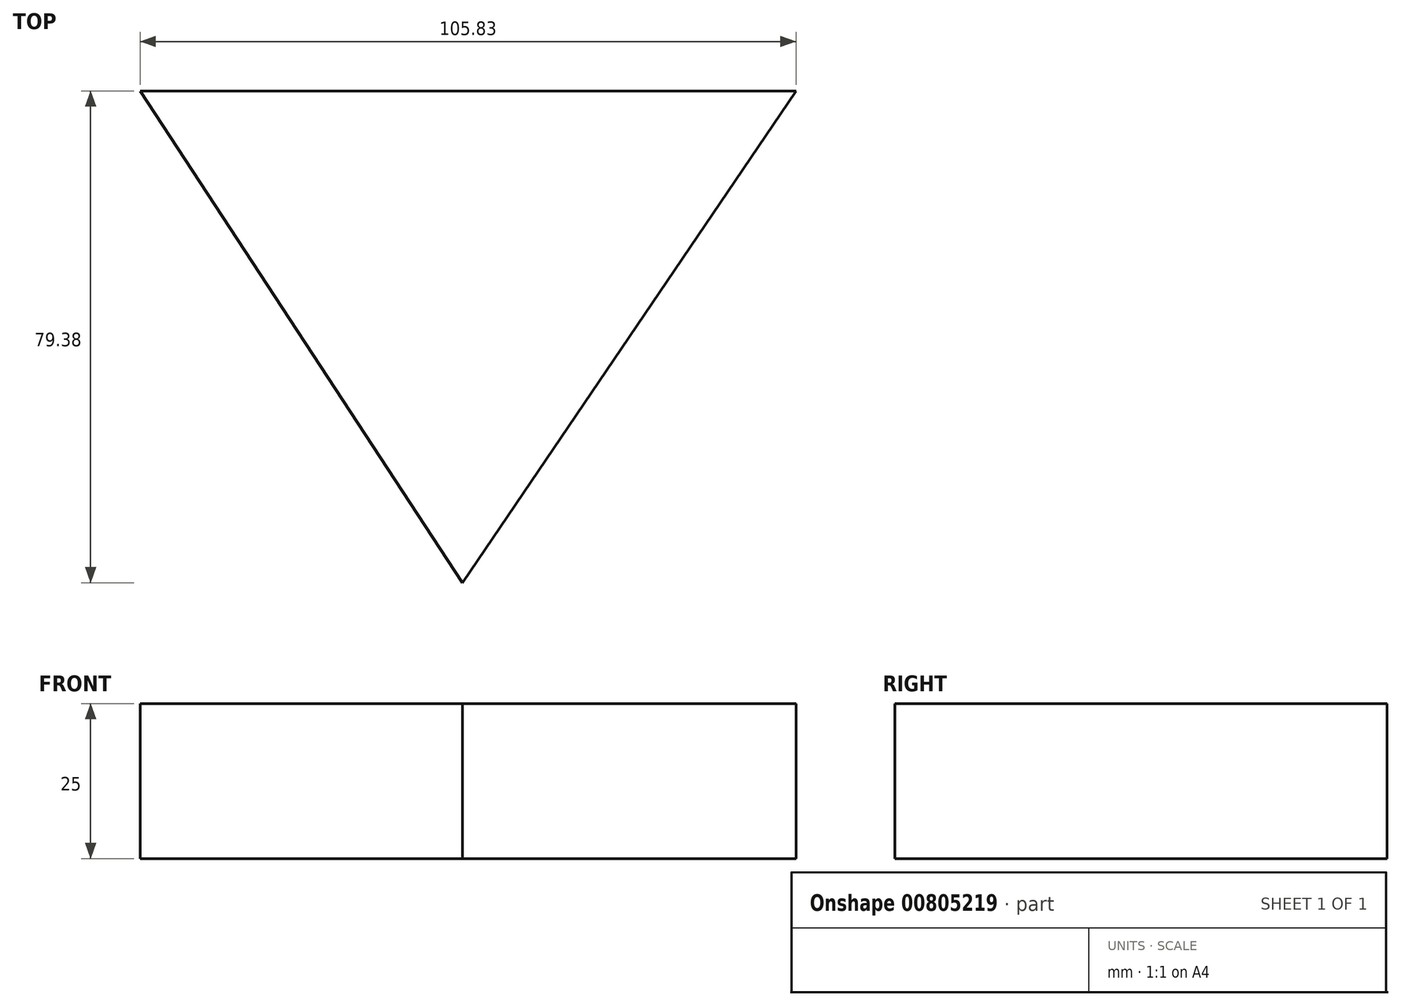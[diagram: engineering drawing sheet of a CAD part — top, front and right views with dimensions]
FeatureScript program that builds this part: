
annotation { "Feature Type Name" : "Feature", "Feature Type Description" : "" }
export const myFeature = defineFeature(function(context is Context, id is Id, definition is map)
    precondition{}
    {
        {
            var Q0;
            Q0=qCreatedBy(makeId("Top.planeOp"),FACE);
            var sketch = newSketch(context, id + "F0", { "sketchPlane" : qUnion([Q0])});
            skLineSegment(sketch, "E0", {"start": v(-52.01, 32.86) * mm, "end": v(53.82, 32.86) * mm});
            skLineSegment(sketch, "E1", {"start": v(53.82, 32.86) * mm, "end": v(0, -46.52) * mm});
            skLineSegment(sketch, "E2", {"start": v(-52.01, 32.86) * mm, "end": v(0, -46.52) * mm});
            skSolve(sketch);
        }
        {
            var Q0;
            Q0=sQuery(id+"F0.wireOp",EDGE,"E1");
            var Q1;
            Q1=sQuery(id+"F0.wireOp",EDGE,"E0");
            var Q2;
            Q2=sQuery(id+"F0.wireOp",EDGE,"E2");
            extrude(context, id + "F1", {"bodyType" : ToolBodyType.SURFACE, "surfaceEntities" : qUnion([Q0, Q1, Q2]), "depth" : 25 * mm, "offsetDistance" : 25 * mm});
        }
    });
